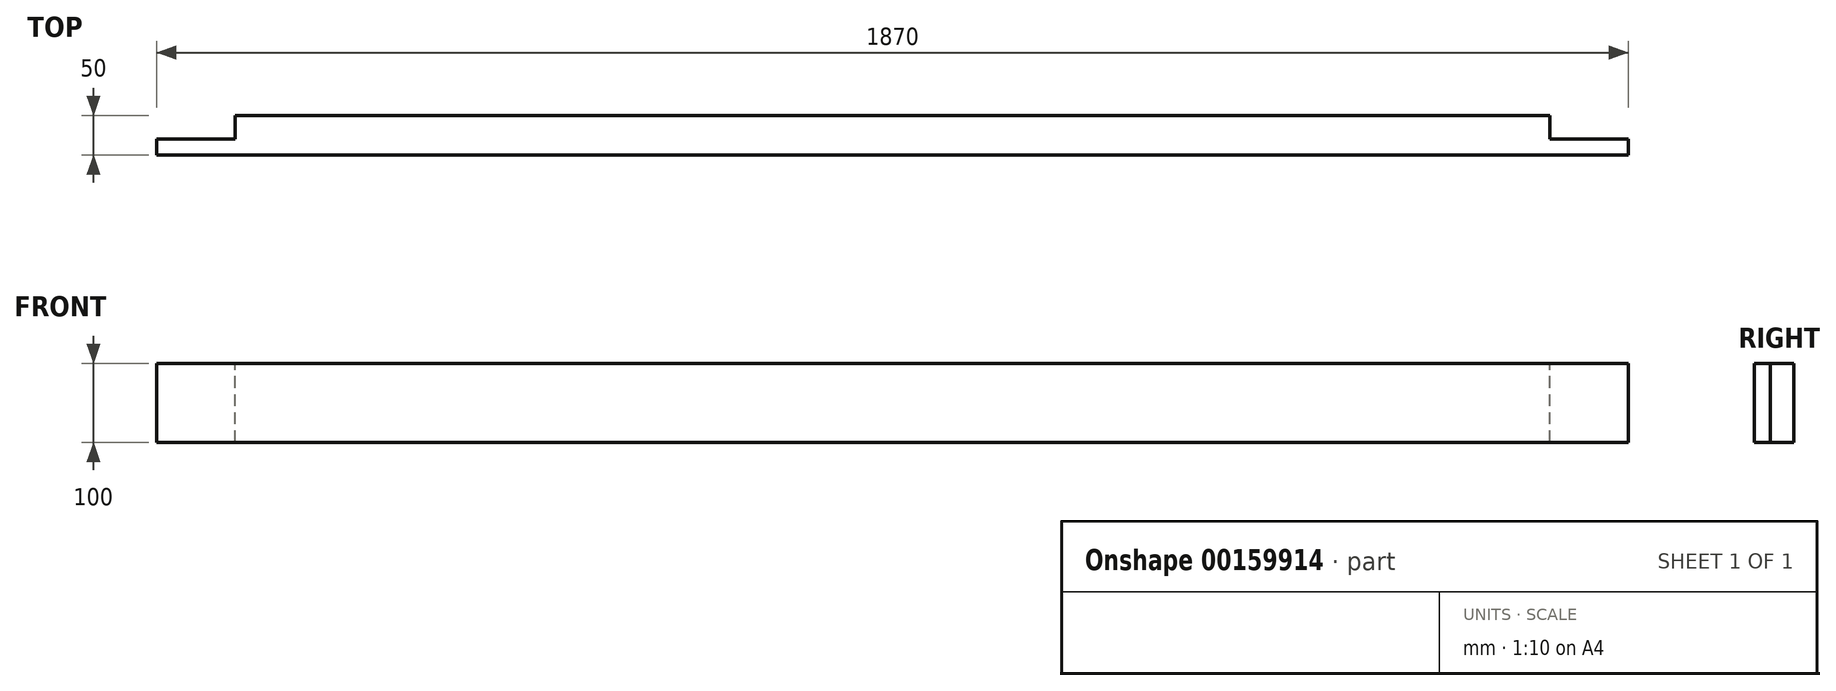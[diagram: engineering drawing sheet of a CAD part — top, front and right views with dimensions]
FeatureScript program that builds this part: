
annotation { "Feature Type Name" : "Feature", "Feature Type Description" : "" }
export const myFeature = defineFeature(function(context is Context, id is Id, definition is map)
    precondition{}
    {
        {
            assignVariable(context, id + "F0", {"name" : "L", "anyValue" : 1870 * mm});
        }
        {
            var Q0;
            Q0=qCreatedBy(makeId("Right.planeOp"),FACE);
            var sketch = newSketch(context, id + "F1", { "sketchPlane" : qUnion([Q0])});
            skLineSegment(sketch, "E0.bottom", {"start": v(-25, 50) * mm, "end": v(25, 50) * mm});
            skLineSegment(sketch, "E0.top", {"start": v(-25, -50) * mm, "end": v(25, -50) * mm});
            skLineSegment(sketch, "E0.left", {"start": v(-25, 50) * mm, "end": v(-25, -50) * mm});
            skLineSegment(sketch, "E0.right", {"start": v(25, 50) * mm, "end": v(25, -50) * mm});
            skPoint(sketch, "E0.middle", {"position": v(0, 0) * mm});
            skSolve(sketch);
        }
        {
            var Q0;
            Q0=makeQuery(id+"F1.imprint","IMPRINT",FACE,{"disambiguationData":[TD([[makeQuery(id+"F1.imprint","IMPRINT",EDGE,{"derivedFrom":sQuery(id+"F1.wireOp",EDGE,"E0.bottom")}),-1.0]])]});
            var Q1;
            Q1 = qConstructionFilter(qBodyType(qCreatedBy(id + "F1" ,EDGE), BodyType.WIRE), ConstructionObject.NO);
            extrude(context, id + "F2", {"entities" : qUnion([Q0]), "surfaceEntities" : qUnion([Q1]), "endBound" : BoundingType.SYMMETRIC, "depth" : getVariable(context, 'L')});
        }
        {
            var Q0;
            Q0=makeQuery(id+"F2.opExtrude","SWEPT_FACE",FACE,{"disambiguationData":[OSD([sQuery(id+"F1.wireOp",EDGE,"E0.bottom")])]});
            var sketch = newSketch(context, id + "F3", { "sketchPlane" : qUnion([Q0])});
            skLineSegment(sketch, "E1.bottom", {"start": v(-935, 25) * mm, "end": v(-835, 25) * mm});
            skLineSegment(sketch, "E1.top", {"start": v(-935, -5) * mm, "end": v(-835, -5) * mm});
            skLineSegment(sketch, "E1.left", {"start": v(-935, 25) * mm, "end": v(-935, -5) * mm});
            skLineSegment(sketch, "E1.right", {"start": v(-835, 25) * mm, "end": v(-835, -5) * mm});
            skLineSegment(sketch, "E2.MirrorCS", {"start": v(935, 25) * mm, "end": v(835, 25) * mm});
            skLineSegment(sketch, "E3.MirrorCS", {"start": v(835, 25) * mm, "end": v(835, -5) * mm});
            skLineSegment(sketch, "E4.MirrorCS", {"start": v(935, -5) * mm, "end": v(835, -5) * mm});
            skLineSegment(sketch, "E5.MirrorCS", {"start": v(935, 25) * mm, "end": v(935, -5) * mm});
            skSolve(sketch);
        }
        {
            var Q0;
            Q0 = qSketchRegion(id + "F3", true);
            extrude(context, id + "F4", {"entities" : qUnion([Q0]), "operationType" : NewBodyOperationType.REMOVE, "endBound" : BoundingType.THROUGH_ALL, "oppositeDirection" : true, "depth" : 25 * mm});
        }
    });
